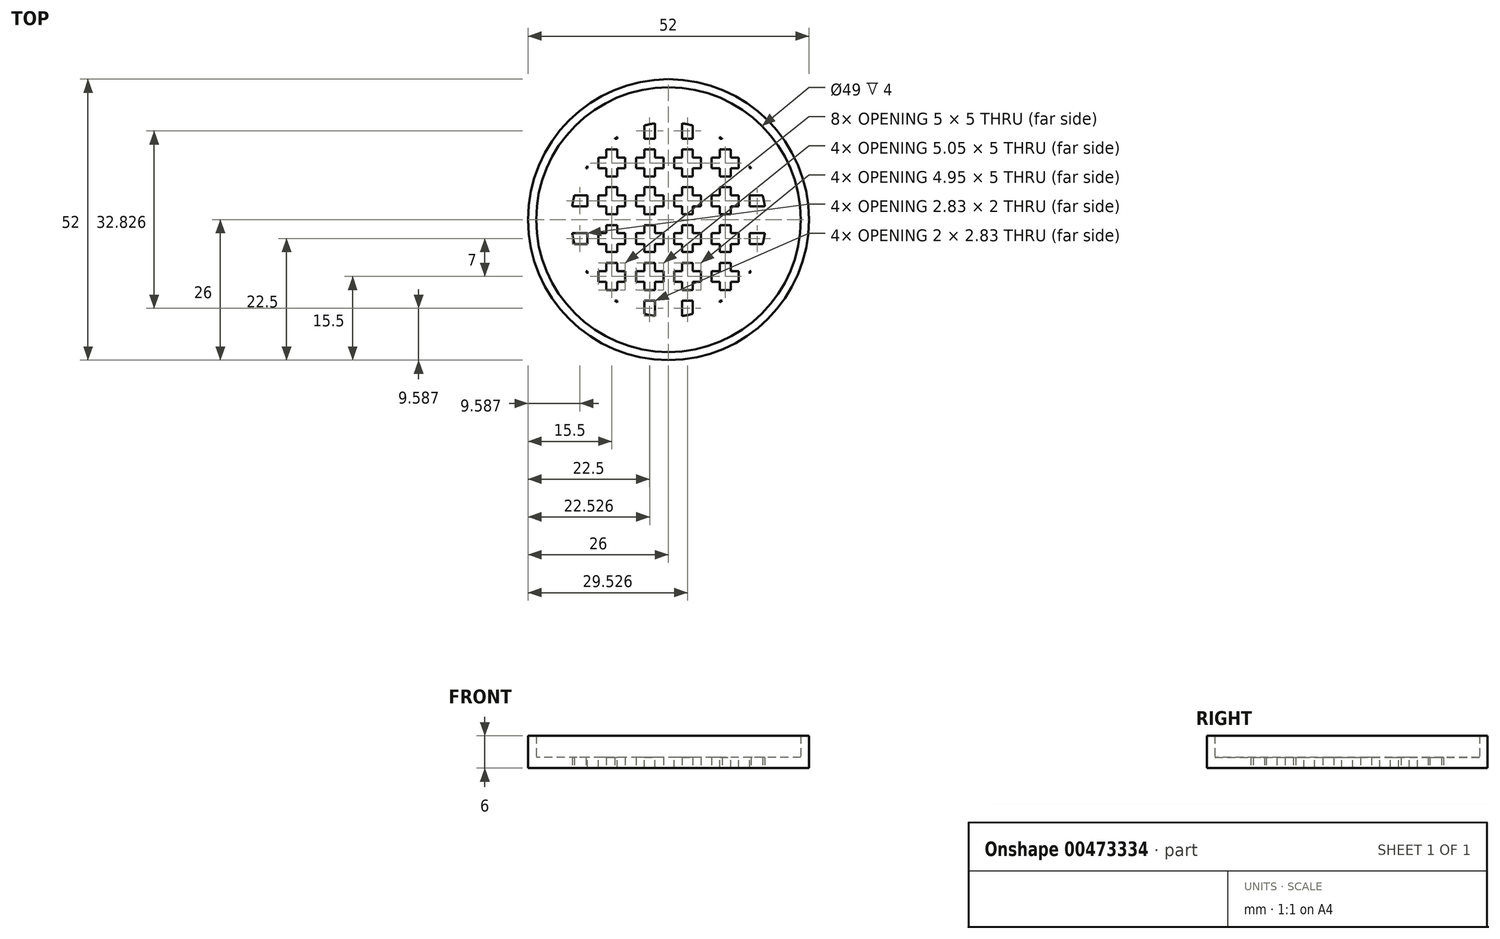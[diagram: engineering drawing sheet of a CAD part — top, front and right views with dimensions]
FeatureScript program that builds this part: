
annotation { "Feature Type Name" : "Feature", "Feature Type Description" : "" }
export const myFeature = defineFeature(function(context is Context, id is Id, definition is map)
    precondition{}
    {
        {
            var Q0;
            Q0=qCreatedBy(makeId("Top.planeOp"),FACE);
            var sketch = newSketch(context, id + "F0", { "sketchPlane" : qUnion([Q0])});
            skCircle(sketch, "E0", {"center": v(0, 0) * mm, "radius": 18 * mm});
            skSolve(sketch);
        }
        {
            var Q0;
            Q0 = qSketchRegion(id + "F0", true);
            extrude(context, id + "F1", {"entities" : qUnion([Q0]), "depth" : 2 * mm});
        }
        {
            var Q0;
            Q0=qCreatedBy(makeId("Top.planeOp"),FACE);
            var sketch = newSketch(context, id + "F2", { "sketchPlane" : qUnion([Q0])});
            skLineSegment(sketch, "E1.bottom", {"start": v(-11.5, 15.29) * mm, "end": v(-9.5, 15.29) * mm});
            skLineSegment(sketch, "E1.top", {"start": v(-11.5, -15.29) * mm, "end": v(-9.5, -15.29) * mm});
            skLineSegment(sketch, "E1.left", {"start": v(-11.5, 15.29) * mm, "end": v(-11.5, -15.29) * mm});
            skLineSegment(sketch, "E1.right", {"start": v(-9.5, 15.29) * mm, "end": v(-9.5, -15.29) * mm});
            skLineSegment(sketch, "E2.bottom", {"start": v(-4.5, 18) * mm, "end": v(-2.5, 18) * mm});
            skLineSegment(sketch, "E2.top", {"start": v(-4.5, -18) * mm, "end": v(-2.5, -18) * mm});
            skLineSegment(sketch, "E2.left", {"start": v(-4.5, 18) * mm, "end": v(-4.5, -18) * mm});
            skLineSegment(sketch, "E2.right", {"start": v(-2.5, 18) * mm, "end": v(-2.5, -18) * mm});
            skLineSegment(sketch, "E3.bottom", {"start": v(2.5, 18) * mm, "end": v(4.5, 18) * mm});
            skLineSegment(sketch, "E3.top", {"start": v(2.5, -18) * mm, "end": v(4.5, -18) * mm});
            skLineSegment(sketch, "E3.left", {"start": v(2.5, 18) * mm, "end": v(2.5, -18) * mm});
            skLineSegment(sketch, "E3.right", {"start": v(4.5, 18) * mm, "end": v(4.5, -18) * mm});
            skLineSegment(sketch, "E4.bottom", {"start": v(9.5, 15.29) * mm, "end": v(11.5, 15.29) * mm});
            skLineSegment(sketch, "E4.top", {"start": v(9.5, -15.29) * mm, "end": v(11.5, -15.29) * mm});
            skLineSegment(sketch, "E4.left", {"start": v(9.5, 15.29) * mm, "end": v(9.5, -15.29) * mm});
            skLineSegment(sketch, "E4.right", {"start": v(11.5, 15.29) * mm, "end": v(11.5, -15.29) * mm});
            skLineSegment(sketch, "E5.bottom", {"start": v(-15.29, -9.5) * mm, "end": v(15.29, -9.5) * mm});
            skLineSegment(sketch, "E5.top", {"start": v(-15.29, -11.5) * mm, "end": v(15.29, -11.5) * mm});
            skLineSegment(sketch, "E5.left", {"start": v(-15.29, -9.5) * mm, "end": v(-15.29, -11.5) * mm});
            skLineSegment(sketch, "E5.right", {"start": v(15.29, -9.5) * mm, "end": v(15.29, -11.5) * mm});
            skLineSegment(sketch, "E6.bottom", {"start": v(-17.83, -2.5) * mm, "end": v(17.83, -2.5) * mm});
            skLineSegment(sketch, "E6.top", {"start": v(-17.83, -4.5) * mm, "end": v(17.83, -4.5) * mm});
            skLineSegment(sketch, "E6.left", {"start": v(-17.83, -2.5) * mm, "end": v(-17.83, -4.5) * mm});
            skLineSegment(sketch, "E6.right", {"start": v(17.83, -2.5) * mm, "end": v(17.83, -4.5) * mm});
            skLineSegment(sketch, "E7.bottom", {"start": v(-21.9, 4.5) * mm, "end": v(17.83, 4.5) * mm});
            skLineSegment(sketch, "E7.top", {"start": v(-21.9, 2.5) * mm, "end": v(17.83, 2.5) * mm});
            skLineSegment(sketch, "E7.left", {"start": v(-21.9, 4.5) * mm, "end": v(-21.9, 2.5) * mm});
            skLineSegment(sketch, "E7.right", {"start": v(17.83, 4.5) * mm, "end": v(17.83, 2.5) * mm});
            skLineSegment(sketch, "E8.bottom", {"start": v(-15.29, 11.5) * mm, "end": v(15.29, 11.5) * mm});
            skLineSegment(sketch, "E8.top", {"start": v(-15.29, 9.5) * mm, "end": v(15.29, 9.5) * mm});
            skLineSegment(sketch, "E8.left", {"start": v(-15.29, 11.5) * mm, "end": v(-15.29, 9.5) * mm});
            skLineSegment(sketch, "E8.right", {"start": v(15.29, 11.5) * mm, "end": v(15.29, 9.5) * mm});
            skSolve(sketch);
        }
        {
            var Q0;
            Q0 = qSketchRegion(id + "F2", true);
            extrude(context, id + "F3", {"entities" : qUnion([Q0]), "operationType" : NewBodyOperationType.REMOVE, "depth" : 25 * mm});
        }
        {
            var Q0;
            Q0=qCreatedBy(makeId("Top.planeOp"),FACE);
            var sketch = newSketch(context, id + "F4", { "sketchPlane" : qUnion([Q0])});
            skCircle(sketch, "E9", {"center": v(0, 0) * mm, "radius": 26 * mm});
            skCircle(sketch, "E10", {"center": v(0, 0) * mm, "radius": 18 * mm});
            skSolve(sketch);
        }
        {
            var Q0;
            Q0 = qSketchRegion(id + "F4", true);
            extrude(context, id + "F5", {"entities" : qUnion([Q0]), "operationType" : NewBodyOperationType.ADD, "depth" : 2 * mm});
        }
        {
            var Q0;
            Q0=qCreatedBy(makeId("Top.planeOp"),FACE);
            var sketch = newSketch(context, id + "F6", { "sketchPlane" : qUnion([Q0])});
            skLineSegment(sketch, "E11.bottom", {"start": v(-4.29, 9.5) * mm, "end": v(-2.29, 9.5) * mm});
            skLineSegment(sketch, "E11.top", {"start": v(-4.29, -5.46) * mm, "end": v(-2.29, -5.46) * mm});
            skLineSegment(sketch, "E11.left", {"start": v(-4.29, 9.5) * mm, "end": v(-4.29, -5.46) * mm});
            skLineSegment(sketch, "E11.right", {"start": v(-2.29, 9.5) * mm, "end": v(-2.29, -5.46) * mm});
            skSolve(sketch);
        }
        {
            var Q0;
            Q0 = qSketchRegion(id + "F6", true);
            extrude(context, id + "F7", {"entities" : qUnion([Q0]), "operationType" : NewBodyOperationType.REMOVE, "oppositeDirection" : true, "depth" : 25 * mm});
        }
        {
            var Q0;
            Q0=qCreatedBy(makeId("Top.planeOp"),FACE);
            var sketch = newSketch(context, id + "F8", { "sketchPlane" : qUnion([Q0])});
            skLineSegment(sketch, "E12.bottom", {"start": v(-4.5, 11.5) * mm, "end": v(-2.5, 11.5) * mm});
            skLineSegment(sketch, "E12.top", {"start": v(-4.5, -11.5) * mm, "end": v(-2.5, -11.5) * mm});
            skLineSegment(sketch, "E12.left", {"start": v(-4.5, 11.5) * mm, "end": v(-4.5, -11.5) * mm});
            skLineSegment(sketch, "E12.right", {"start": v(-2.5, 11.5) * mm, "end": v(-2.5, -11.5) * mm});
            skLineSegment(sketch, "E13.bottom", {"start": v(2.5, 11.5) * mm, "end": v(4.5, 11.5) * mm});
            skLineSegment(sketch, "E13.top", {"start": v(2.5, -11.5) * mm, "end": v(4.5, -11.5) * mm});
            skLineSegment(sketch, "E13.left", {"start": v(2.5, 11.5) * mm, "end": v(2.5, -11.5) * mm});
            skLineSegment(sketch, "E13.right", {"start": v(4.5, 11.5) * mm, "end": v(4.5, -11.5) * mm});
            skLineSegment(sketch, "E14.bottom", {"start": v(-11.5, 4.5) * mm, "end": v(11.5, 4.5) * mm});
            skLineSegment(sketch, "E14.top", {"start": v(-11.5, 2.5) * mm, "end": v(11.5, 2.5) * mm});
            skLineSegment(sketch, "E14.left", {"start": v(-11.5, 4.5) * mm, "end": v(-11.5, 2.5) * mm});
            skLineSegment(sketch, "E14.right", {"start": v(11.5, 4.5) * mm, "end": v(11.5, 2.5) * mm});
            skLineSegment(sketch, "E15.bottom", {"start": v(-11.5, -2.5) * mm, "end": v(11.5, -2.5) * mm});
            skLineSegment(sketch, "E15.top", {"start": v(-11.5, -4.5) * mm, "end": v(11.5, -4.5) * mm});
            skLineSegment(sketch, "E15.left", {"start": v(-11.5, -2.5) * mm, "end": v(-11.5, -4.5) * mm});
            skLineSegment(sketch, "E15.right", {"start": v(11.5, -2.5) * mm, "end": v(11.5, -4.5) * mm});
            skSolve(sketch);
        }
        {
            var Q0;
            Q0 = qSketchRegion(id + "F8", true);
            extrude(context, id + "F9", {"entities" : qUnion([Q0]), "operationType" : NewBodyOperationType.REMOVE, "depth" : 25 * mm});
        }
        {
            var Q0;
            Q0=qCreatedBy(makeId("Top.planeOp"),FACE);
            var sketch = newSketch(context, id + "F10", { "sketchPlane" : qUnion([Q0])});
            skLineSegment(sketch, "E16.bottom", {"start": v(-15, 8) * mm, "end": v(15.3, 8) * mm});
            skLineSegment(sketch, "E16.top", {"start": v(-15, 6) * mm, "end": v(15.3, 6) * mm});
            skLineSegment(sketch, "E16.left", {"start": v(-15, 8) * mm, "end": v(-15, 6) * mm});
            skLineSegment(sketch, "E16.right", {"start": v(15.3, 8) * mm, "end": v(15.3, 6) * mm});
            skLineSegment(sketch, "E17.bottom", {"start": v(-13.95, 1) * mm, "end": v(13.98, 1) * mm});
            skLineSegment(sketch, "E17.top", {"start": v(-13.95, -1) * mm, "end": v(13.98, -1) * mm});
            skLineSegment(sketch, "E17.left", {"start": v(-13.95, 1) * mm, "end": v(-13.95, -1) * mm});
            skLineSegment(sketch, "E17.right", {"start": v(13.98, 1) * mm, "end": v(13.98, -1) * mm});
            skLineSegment(sketch, "E18.bottom", {"start": v(-13.75, -6) * mm, "end": v(12.64, -6) * mm});
            skLineSegment(sketch, "E18.top", {"start": v(-13.75, -8) * mm, "end": v(12.64, -8) * mm});
            skLineSegment(sketch, "E18.left", {"start": v(-13.75, -6) * mm, "end": v(-13.75, -8) * mm});
            skLineSegment(sketch, "E18.right", {"start": v(12.64, -6) * mm, "end": v(12.64, -8) * mm});
            skLineSegment(sketch, "E19.bottom", {"start": v(-10.45, -13) * mm, "end": v(12.45, -13) * mm});
            skLineSegment(sketch, "E19.top", {"start": v(-10.45, -15) * mm, "end": v(12.45, -15) * mm});
            skLineSegment(sketch, "E19.left", {"start": v(-10.45, -13) * mm, "end": v(-10.45, -15) * mm});
            skLineSegment(sketch, "E19.right", {"start": v(12.45, -13) * mm, "end": v(12.45, -15) * mm});
            skLineSegment(sketch, "E20.bottom", {"start": v(-12.51, 13) * mm, "end": v(12.95, 13) * mm});
            skLineSegment(sketch, "E20.top", {"start": v(-12.51, 15) * mm, "end": v(12.95, 15) * mm});
            skLineSegment(sketch, "E20.left", {"start": v(-12.51, 13) * mm, "end": v(-12.51, 15) * mm});
            skLineSegment(sketch, "E20.right", {"start": v(12.95, 13) * mm, "end": v(12.95, 15) * mm});
            skLineSegment(sketch, "E21.bottom", {"start": v(-6, 16.97) * mm, "end": v(-8, 16.97) * mm});
            skLineSegment(sketch, "E21.top", {"start": v(-6, -16.97) * mm, "end": v(-8, -16.97) * mm});
            skLineSegment(sketch, "E21.left", {"start": v(-6, 16.97) * mm, "end": v(-6, -16.97) * mm});
            skLineSegment(sketch, "E21.right", {"start": v(-8, 16.97) * mm, "end": v(-8, -16.97) * mm});
            skPoint(sketch, "E22.oppositeSnap0", {"position": v(1, -15) * mm});
            skLineSegment(sketch, "E22.bottom", {"start": v(-1, 17.97) * mm, "end": v(1, 17.97) * mm});
            skLineSegment(sketch, "E22.top", {"start": v(-1, -17.97) * mm, "end": v(1, -17.97) * mm});
            skLineSegment(sketch, "E22.left", {"start": v(-1, 17.97) * mm, "end": v(-1, -17.97) * mm});
            skLineSegment(sketch, "E22.right", {"start": v(1, 17.97) * mm, "end": v(1, -17.97) * mm});
            skLineSegment(sketch, "E23.bottom", {"start": v(6, 16.97) * mm, "end": v(8, 16.97) * mm});
            skLineSegment(sketch, "E23.top", {"start": v(6, -16.97) * mm, "end": v(8, -16.97) * mm});
            skLineSegment(sketch, "E23.left", {"start": v(6, 16.97) * mm, "end": v(6, -16.97) * mm});
            skLineSegment(sketch, "E23.right", {"start": v(8, 16.97) * mm, "end": v(8, -16.97) * mm});
            skLineSegment(sketch, "E24.bottom", {"start": v(13, -12.45) * mm, "end": v(15, -12.45) * mm});
            skLineSegment(sketch, "E24.top", {"start": v(13, 12.45) * mm, "end": v(15, 12.45) * mm});
            skLineSegment(sketch, "E24.left", {"start": v(13, -12.45) * mm, "end": v(13, 12.45) * mm});
            skLineSegment(sketch, "E24.right", {"start": v(15, -12.45) * mm, "end": v(15, 12.45) * mm});
            skLineSegment(sketch, "E25.bottom", {"start": v(-13, -12.45) * mm, "end": v(-15, -12.45) * mm});
            skLineSegment(sketch, "E25.top", {"start": v(-13, 12.45) * mm, "end": v(-15, 12.45) * mm});
            skLineSegment(sketch, "E25.left", {"start": v(-13, -12.45) * mm, "end": v(-13, 12.45) * mm});
            skLineSegment(sketch, "E25.right", {"start": v(-15, -12.45) * mm, "end": v(-15, 12.45) * mm});
            skSolve(sketch);
        }
        {
            var Q0;
            Q0 = qSketchRegion(id + "F10", true);
            extrude(context, id + "F11", {"entities" : qUnion([Q0]), "operationType" : NewBodyOperationType.ADD, "depth" : 2 * mm});
        }
        {
            var Q0;
            Q0=qCreatedBy(makeId("Top.planeOp"),FACE);
            var sketch = newSketch(context, id + "F12", { "sketchPlane" : qUnion([Q0])});
            skLineSegment(sketch, "E26.bottom", {"start": v(-8, 9.5) * mm, "end": v(-6, 9.5) * mm});
            skLineSegment(sketch, "E26.top", {"start": v(-8, -7.23) * mm, "end": v(-6, -7.23) * mm});
            skLineSegment(sketch, "E26.left", {"start": v(-8, 9.5) * mm, "end": v(-8, -7.23) * mm});
            skLineSegment(sketch, "E26.right", {"start": v(-6, 9.5) * mm, "end": v(-6, -7.23) * mm});
            skLineSegment(sketch, "E27.bottom", {"start": v(-0.95, -11.5) * mm, "end": v(1.05, -11.5) * mm});
            skLineSegment(sketch, "E27.top", {"start": v(-0.95, 12.4) * mm, "end": v(1.05, 12.4) * mm});
            skLineSegment(sketch, "E27.left", {"start": v(-0.95, -11.5) * mm, "end": v(-0.95, 12.4) * mm});
            skLineSegment(sketch, "E27.right", {"start": v(1.05, -11.5) * mm, "end": v(1.05, 12.4) * mm});
            skLineSegment(sketch, "E28.bottom", {"start": v(6, 6) * mm, "end": v(8, 6) * mm});
            skLineSegment(sketch, "E28.top", {"start": v(6, -1.53) * mm, "end": v(8, -1.53) * mm});
            skLineSegment(sketch, "E28.left", {"start": v(6, 6) * mm, "end": v(6, -1.53) * mm});
            skLineSegment(sketch, "E28.right", {"start": v(8, 6) * mm, "end": v(8, -1.53) * mm});
            skPoint(sketch, "E29.oppositeSnap0", {"position": v(7, 6) * mm});
            skLineSegment(sketch, "E29.bottom", {"start": v(-9.5, 8) * mm, "end": v(10.5, 8) * mm});
            skLineSegment(sketch, "E29.top", {"start": v(-9.5, 6) * mm, "end": v(10.5, 6) * mm});
            skLineSegment(sketch, "E29.left", {"start": v(-9.5, 8) * mm, "end": v(-9.5, 6) * mm});
            skLineSegment(sketch, "E29.right", {"start": v(10.5, 8) * mm, "end": v(10.5, 6) * mm});
            skLineSegment(sketch, "E30.bottom", {"start": v(-12.5, 1) * mm, "end": v(11.5, 1) * mm});
            skLineSegment(sketch, "E30.top", {"start": v(-12.5, -1) * mm, "end": v(11.5, -1) * mm});
            skLineSegment(sketch, "E30.left", {"start": v(-12.5, 1) * mm, "end": v(-12.5, -1) * mm});
            skLineSegment(sketch, "E30.right", {"start": v(11.5, 1) * mm, "end": v(11.5, -1) * mm});
            skLineSegment(sketch, "E31.bottom", {"start": v(-9.5, -6) * mm, "end": v(10.5, -6) * mm});
            skLineSegment(sketch, "E31.top", {"start": v(-9.5, -8) * mm, "end": v(10.5, -8) * mm});
            skLineSegment(sketch, "E31.left", {"start": v(-9.5, -6) * mm, "end": v(-9.5, -8) * mm});
            skLineSegment(sketch, "E31.right", {"start": v(10.5, -6) * mm, "end": v(10.5, -8) * mm});
            skSolve(sketch);
        }
        {
            var Q0;
            Q0 = qSketchRegion(id + "F12", true);
            extrude(context, id + "F13", {"entities" : qUnion([Q0]), "operationType" : NewBodyOperationType.ADD, "depth" : 2 * mm});
        }
        {
            var Q0;
            Q0=qCreatedBy(makeId("Top.planeOp"),FACE);
            var sketch = newSketch(context, id + "F14", { "sketchPlane" : qUnion([Q0])});
            skLineSegment(sketch, "E32.bottom", {"start": v(-0.95, 5.83) * mm, "end": v(1.05, 5.83) * mm});
            skLineSegment(sketch, "E32.top", {"start": v(-0.95, 0) * mm, "end": v(1.05, 0) * mm});
            skLineSegment(sketch, "E32.left", {"start": v(-0.95, 5.83) * mm, "end": v(-0.95, 0) * mm});
            skLineSegment(sketch, "E32.right", {"start": v(1.05, 5.83) * mm, "end": v(1.05, 0) * mm});
            skLineSegment(sketch, "E33.bottom", {"start": v(-6.66, 1) * mm, "end": v(-1.89, 1) * mm});
            skLineSegment(sketch, "E33.top", {"start": v(-6.66, -1) * mm, "end": v(-1.89, -1) * mm});
            skLineSegment(sketch, "E33.left", {"start": v(-6.66, 1) * mm, "end": v(-6.66, -1) * mm});
            skLineSegment(sketch, "E33.right", {"start": v(-1.89, 1) * mm, "end": v(-1.89, -1) * mm});
            skLineSegment(sketch, "E34.bottom", {"start": v(-7.18, -13) * mm, "end": v(-12.23, -13) * mm});
            skLineSegment(sketch, "E34.top", {"start": v(-7.18, -15) * mm, "end": v(-12.23, -15) * mm});
            skLineSegment(sketch, "E34.left", {"start": v(-7.18, -13) * mm, "end": v(-7.18, -15) * mm});
            skLineSegment(sketch, "E34.right", {"start": v(-12.23, -13) * mm, "end": v(-12.23, -15) * mm});
            skSolve(sketch);
        }
        {
            var Q0;
            Q0 = qSketchRegion(id + "F14", true);
            extrude(context, id + "F15", {"entities" : qUnion([Q0]), "operationType" : NewBodyOperationType.ADD, "depth" : 2 * mm});
        }
        {
            var Q0;
            {var subQ0=sQuery(id+"F2.wireOp",EDGE,"E6.top");var subQ5=sQuery(id+"F2.wireOp",EDGE,"E6.bottom");var subQ7=sQuery(id+"F2.wireOp",EDGE,"E7.top");var subQ9=sQuery(id+"F2.wireOp",EDGE,"E7.bottom");var subQ11=sQuery(id+"F2.wireOp",EDGE,"E8.top");var subQ15=sQuery(id+"F2.wireOp",EDGE,"E3.right");var subQ19=sQuery(id+"F2.wireOp",EDGE,"E2.right");var subQ23=sQuery(id+"F2.wireOp",EDGE,"E1.right");var subQ27=sQuery(id+"F8.wireOp",EDGE,"E13.right");var subQ28=sQuery(id+"F8.wireOp",EDGE,"E13.top");var subQ32=makeQuery(id+"F2.imprint","INTERSECT",VERTEX,{"derivedFrom":[subQ23,subQ0]});var subQ33=makeQuery(id+"F2.imprint","INTERSECT",VERTEX,{"derivedFrom":[subQ23,subQ5]});var subQ34=makeQuery(id+"F2.imprint","INTERSECT",VERTEX,{"derivedFrom":[subQ23,subQ7]});var subQ35=makeQuery(id+"F2.imprint","INTERSECT",VERTEX,{"derivedFrom":[subQ23,subQ9]});var subQ36=makeQuery(id+"F2.imprint","INTERSECT",VERTEX,{"derivedFrom":[subQ23,subQ11]});var subQ37=makeQuery(id+"F3.opExtrude","SWEPT_FACE",FACE,{"disambiguationData":[OSD([subQ23]),TDD([makeQuery(id+"F2.imprint","IMPRINT",EDGE,{"disambiguationData":[TD([[subQ36,-1.0]])],"derivedFrom":subQ23}),makeQuery(id+"F2.imprint","IMPRINT",EDGE,{"disambiguationData":[TD([[subQ35,-1.0]])],"derivedFrom":subQ23}),makeQuery(id+"F2.imprint","IMPRINT",EDGE,{"disambiguationData":[TD([[subQ34,-1.0]])],"derivedFrom":subQ23}),makeQuery(id+"F2.imprint","IMPRINT",EDGE,{"disambiguationData":[TD([[subQ33,-1.0]])],"derivedFrom":subQ23}),makeQuery(id+"F2.imprint","IMPRINT",EDGE,{"disambiguationData":[TD([[subQ32,-1.0]])],"derivedFrom":subQ23})])]});var subQ43=sQuery(id+"F0.wireOp",EDGE,"E0");var subQ44=makeQuery(id+"F1.opExtrude","CAP_FACE",FACE,{"disambiguationData":[OSD([subQ43])],"isStart":false});var subQ45=makeQuery(id+"F3.boolean.opBoolean","SPLIT",FACE,{"disambiguationData":[TD([subQ37])],"derivedFrom":subQ44});var subQ47=sQuery(id+"F8.wireOp",EDGE,"E13.bottom");var subQ52=sQuery(id+"F8.wireOp",EDGE,"E12.left");var subQ53=sQuery(id+"F8.wireOp",EDGE,"E12.top");var subQ58=sQuery(id+"F8.wireOp",EDGE,"E12.bottom");var subQ59=sQuery(id+"F8.wireOp",EDGE,"E14.top");var subQ60=makeQuery(id+"F8.imprint","INTERSECT",VERTEX,{"derivedFrom":[subQ27,subQ59]});var subQ64=sQuery(id+"F2.wireOp",EDGE,"E4.right");var subQ65=makeQuery(id+"F2.imprint","INTERSECT",VERTEX,{"derivedFrom":[subQ64,subQ0]});var subQ69=makeQuery(id+"F2.imprint","INTERSECT",VERTEX,{"derivedFrom":[subQ64,subQ7]});var subQ72=makeQuery(id+"F2.imprint","INTERSECT",VERTEX,{"derivedFrom":[subQ64,subQ11]});var subQ75=sQuery(id+"F2.wireOp",EDGE,"E3.top");var subQ78=sQuery(id+"F2.wireOp",EDGE,"E4.top");var subQ80=sQuery(id+"F2.wireOp",EDGE,"E3.bottom");var subQ83=sQuery(id+"F2.wireOp",EDGE,"E4.bottom");var subQ85=sQuery(id+"F2.wireOp",EDGE,"E2.top");var subQ88=sQuery(id+"F2.wireOp",EDGE,"E2.bottom");var subQ91=sQuery(id+"F2.wireOp",EDGE,"E1.top");var subQ96=sQuery(id+"F2.wireOp",EDGE,"E1.bottom");var subQ97=sQuery(id+"F2.wireOp",EDGE,"E1.left");var subQ98=makeQuery(id+"F2.imprint","INTERSECT",VERTEX,{"derivedFrom":[subQ97,subQ0]});var subQ103=makeQuery(id+"F2.imprint","INTERSECT",VERTEX,{"derivedFrom":[subQ97,subQ7]});var subQ105=makeQuery(id+"F2.imprint","INTERSECT",VERTEX,{"derivedFrom":[subQ97,subQ11]});var subQ112=sQuery(id+"F8.wireOp",EDGE,"E12.right");var subQ118=makeQuery(id+"F8.imprint","INTERSECT",VERTEX,{"derivedFrom":[subQ52,subQ59]});var subQ120=makeQuery(id+"F8.imprint","INTERSECT",VERTEX,{"derivedFrom":[subQ112,subQ59]});Q0=makeQuery(id+"F15.boolean.opBoolean","MERGE",FACE,{"derivedFrom":[makeQuery(id+"F13.boolean.opBoolean","MERGE",FACE,{"derivedFrom":[makeQuery(id+"F9.boolean.opBoolean","SPLIT",FACE,{"disambiguationData":[TD([makeQuery(id+"F9.opExtrude","SWEPT_FACE",FACE,{"disambiguationData":[OSD([subQ112]),TDD([makeQuery(id+"F8.imprint","IMPRINT",EDGE,{"disambiguationData":[TD([[subQ120,-1.0]])],"derivedFrom":subQ112})])]})])],"derivedFrom":subQ45}),makeQuery(id+"F9.boolean.opBoolean","SPLIT",FACE,{"disambiguationData":[TD([makeQuery(id+"F9.opExtrude","SWEPT_FACE",FACE,{"disambiguationData":[OSD([subQ52]),TDD([makeQuery(id+"F8.imprint","IMPRINT",EDGE,{"disambiguationData":[TD([[subQ118,-1.0]])],"derivedFrom":subQ52})])]})])],"derivedFrom":subQ45}),makeQuery(id+"F9.boolean.opBoolean","SPLIT",FACE,{"disambiguationData":[TD([makeQuery(id+"F9.opExtrude","SWEPT_FACE",FACE,{"disambiguationData":[OSD([subQ112]),TDD([makeQuery(id+"F8.imprint","IMPRINT",EDGE,{"disambiguationData":[TD([[makeQuery(id+"F8.imprint","INTERSECT",VERTEX,{"derivedFrom":[subQ58,subQ112]}),-1.0]])],"derivedFrom":subQ112})])]})])],"derivedFrom":subQ45}),makeQuery(id+"F9.boolean.opBoolean","SPLIT",FACE,{"disambiguationData":[TD([makeQuery(id+"F9.opExtrude","SWEPT_FACE",FACE,{"disambiguationData":[OSD([subQ112]),TDD([makeQuery(id+"F8.imprint","IMPRINT",EDGE,{"disambiguationData":[TD([[makeQuery(id+"F8.imprint","INTERSECT",VERTEX,{"derivedFrom":[subQ53,subQ112]}),1.0]])],"derivedFrom":subQ112})])]})])],"derivedFrom":subQ45}),makeQuery(id+"F11.boolean.opBoolean","MERGE",FACE,{"derivedFrom":[makeQuery(id+"F5.boolean.opBoolean","MERGE",FACE,{"derivedFrom":[makeQuery(id+"F3.boolean.opBoolean","SPLIT",FACE,{"disambiguationData":[TD([makeQuery(id+"F3.opExtrude","SWEPT_FACE",FACE,{"disambiguationData":[OSD([subQ97]),TDD([makeQuery(id+"F2.imprint","IMPRINT",EDGE,{"disambiguationData":[TD([[makeQuery(id+"F2.imprint","INTERSECT",VERTEX,{"derivedFrom":[subQ96,subQ97]}),-1.0]])],"derivedFrom":subQ97})])]})])],"derivedFrom":subQ44}),makeQuery(id+"F3.boolean.opBoolean","SPLIT",FACE,{"disambiguationData":[TD([makeQuery(id+"F3.opExtrude","SWEPT_FACE",FACE,{"disambiguationData":[OSD([subQ97]),TDD([makeQuery(id+"F2.imprint","IMPRINT",EDGE,{"disambiguationData":[TD([[makeQuery(id+"F2.imprint","INTERSECT",VERTEX,{"derivedFrom":[subQ91,subQ97]}),1.0]])],"derivedFrom":subQ97})])]})])],"derivedFrom":subQ44}),makeQuery(id+"F3.boolean.opBoolean","SPLIT",FACE,{"disambiguationData":[TD([makeQuery(id+"F3.opExtrude","SWEPT_FACE",FACE,{"disambiguationData":[OSD([subQ64]),TDD([makeQuery(id+"F2.imprint","IMPRINT",EDGE,{"disambiguationData":[TD([[makeQuery(id+"F2.imprint","INTERSECT",VERTEX,{"derivedFrom":[subQ83,subQ64]}),-1.0]])],"derivedFrom":subQ64})])]})])],"derivedFrom":subQ44}),makeQuery(id+"F3.boolean.opBoolean","SPLIT",FACE,{"disambiguationData":[TD([makeQuery(id+"F3.opExtrude","SWEPT_FACE",FACE,{"disambiguationData":[OSD([subQ64]),TDD([makeQuery(id+"F2.imprint","IMPRINT",EDGE,{"disambiguationData":[TD([[makeQuery(id+"F2.imprint","INTERSECT",VERTEX,{"derivedFrom":[subQ78,subQ64]}),1.0]])],"derivedFrom":subQ64})])]})])],"derivedFrom":subQ44}),makeQuery(id+"F3.boolean.opBoolean","SPLIT",FACE,{"disambiguationData":[TD([makeQuery(id+"F3.opExtrude","SWEPT_FACE",FACE,{"disambiguationData":[OSD([subQ97]),TDD([makeQuery(id+"F2.imprint","IMPRINT",EDGE,{"disambiguationData":[TD([[subQ105,-1.0]])],"derivedFrom":subQ97})])]})])],"derivedFrom":subQ44}),makeQuery(id+"F3.boolean.opBoolean","SPLIT",FACE,{"disambiguationData":[TD([makeQuery(id+"F3.opExtrude","SWEPT_FACE",FACE,{"disambiguationData":[OSD([subQ97]),TDD([makeQuery(id+"F2.imprint","IMPRINT",EDGE,{"disambiguationData":[TD([[subQ103,-1.0]])],"derivedFrom":subQ97})])]})])],"derivedFrom":subQ44}),makeQuery(id+"F3.boolean.opBoolean","SPLIT",FACE,{"disambiguationData":[TD([makeQuery(id+"F3.opExtrude","SWEPT_FACE",FACE,{"disambiguationData":[OSD([subQ97]),TDD([makeQuery(id+"F2.imprint","IMPRINT",EDGE,{"disambiguationData":[TD([[subQ98,-1.0]])],"derivedFrom":subQ97})])]})])],"derivedFrom":subQ44}),makeQuery(id+"F3.boolean.opBoolean","SPLIT",FACE,{"disambiguationData":[TD([makeQuery(id+"F3.opExtrude","SWEPT_FACE",FACE,{"disambiguationData":[OSD([subQ23]),TDD([makeQuery(id+"F2.imprint","IMPRINT",EDGE,{"disambiguationData":[TD([[makeQuery(id+"F2.imprint","INTERSECT",VERTEX,{"derivedFrom":[subQ96,subQ23]}),-1.0]])],"derivedFrom":subQ23})])]})])],"derivedFrom":subQ44}),makeQuery(id+"F3.boolean.opBoolean","SPLIT",FACE,{"disambiguationData":[TD([makeQuery(id+"F3.opExtrude","SWEPT_FACE",FACE,{"disambiguationData":[OSD([subQ23]),TDD([makeQuery(id+"F2.imprint","IMPRINT",EDGE,{"disambiguationData":[TD([[makeQuery(id+"F2.imprint","INTERSECT",VERTEX,{"derivedFrom":[subQ91,subQ23]}),1.0]])],"derivedFrom":subQ23})])]})])],"derivedFrom":subQ44}),makeQuery(id+"F3.boolean.opBoolean","SPLIT",FACE,{"disambiguationData":[TD([makeQuery(id+"F3.opExtrude","SWEPT_FACE",FACE,{"disambiguationData":[OSD([subQ19]),TDD([makeQuery(id+"F2.imprint","IMPRINT",EDGE,{"disambiguationData":[TD([[makeQuery(id+"F2.imprint","INTERSECT",VERTEX,{"derivedFrom":[subQ88,subQ19]}),-1.0]])],"derivedFrom":subQ19})])]})])],"derivedFrom":subQ44}),makeQuery(id+"F3.boolean.opBoolean","SPLIT",FACE,{"disambiguationData":[TD([makeQuery(id+"F3.opExtrude","SWEPT_FACE",FACE,{"disambiguationData":[OSD([subQ19]),TDD([makeQuery(id+"F2.imprint","IMPRINT",EDGE,{"disambiguationData":[TD([[makeQuery(id+"F2.imprint","INTERSECT",VERTEX,{"derivedFrom":[subQ85,subQ19]}),1.0]])],"derivedFrom":subQ19})])]})])],"derivedFrom":subQ44}),makeQuery(id+"F3.boolean.opBoolean","SPLIT",FACE,{"disambiguationData":[TD([makeQuery(id+"F3.opExtrude","SWEPT_FACE",FACE,{"disambiguationData":[OSD([subQ15]),TDD([makeQuery(id+"F2.imprint","IMPRINT",EDGE,{"disambiguationData":[TD([[makeQuery(id+"F2.imprint","INTERSECT",VERTEX,{"derivedFrom":[subQ80,subQ15]}),-1.0]])],"derivedFrom":subQ15})])]})])],"derivedFrom":subQ44}),makeQuery(id+"F3.boolean.opBoolean","SPLIT",FACE,{"disambiguationData":[TD([makeQuery(id+"F3.opExtrude","SWEPT_FACE",FACE,{"disambiguationData":[OSD([subQ15]),TDD([makeQuery(id+"F2.imprint","IMPRINT",EDGE,{"disambiguationData":[TD([[makeQuery(id+"F2.imprint","INTERSECT",VERTEX,{"derivedFrom":[subQ75,subQ15]}),1.0]])],"derivedFrom":subQ15})])]})])],"derivedFrom":subQ44}),makeQuery(id+"F3.boolean.opBoolean","SPLIT",FACE,{"disambiguationData":[TD([makeQuery(id+"F3.opExtrude","SWEPT_FACE",FACE,{"disambiguationData":[OSD([subQ64]),TDD([makeQuery(id+"F2.imprint","IMPRINT",EDGE,{"disambiguationData":[TD([[subQ72,-1.0]])],"derivedFrom":subQ64})])]})])],"derivedFrom":subQ44}),makeQuery(id+"F3.boolean.opBoolean","SPLIT",FACE,{"disambiguationData":[TD([makeQuery(id+"F3.opExtrude","SWEPT_FACE",FACE,{"disambiguationData":[OSD([subQ64]),TDD([makeQuery(id+"F2.imprint","IMPRINT",EDGE,{"disambiguationData":[TD([[subQ69,-1.0]])],"derivedFrom":subQ64})])]})])],"derivedFrom":subQ44}),makeQuery(id+"F3.boolean.opBoolean","SPLIT",FACE,{"disambiguationData":[TD([makeQuery(id+"F3.opExtrude","SWEPT_FACE",FACE,{"disambiguationData":[OSD([subQ64]),TDD([makeQuery(id+"F2.imprint","IMPRINT",EDGE,{"disambiguationData":[TD([[subQ65,-1.0]])],"derivedFrom":subQ64})])]})])],"derivedFrom":subQ44}),makeQuery(id+"F5.opExtrude","CAP_FACE",FACE,{"disambiguationData":[OSD([sQuery(id+"F4.wireOp",EDGE,"E9"),sQuery(id+"F4.wireOp",EDGE,"E10")])],"isStart":false})]}),makeQuery(id+"F9.boolean.opBoolean","SPLIT",FACE,{"disambiguationData":[TD([makeQuery(id+"F9.opExtrude","SWEPT_FACE",FACE,{"disambiguationData":[OSD([subQ27]),TDD([makeQuery(id+"F8.imprint","IMPRINT",EDGE,{"disambiguationData":[TD([[subQ60,-1.0]])],"derivedFrom":subQ27})])]})])],"derivedFrom":subQ45}),makeQuery(id+"F9.boolean.opBoolean","SPLIT",FACE,{"disambiguationData":[TD([makeQuery(id+"F9.opExtrude","SWEPT_FACE",FACE,{"disambiguationData":[OSD([subQ52]),TDD([makeQuery(id+"F8.imprint","IMPRINT",EDGE,{"disambiguationData":[TD([[makeQuery(id+"F8.imprint","INTERSECT",VERTEX,{"derivedFrom":[subQ58,subQ52]}),-1.0]])],"derivedFrom":subQ52})])]})])],"derivedFrom":subQ45}),makeQuery(id+"F9.boolean.opBoolean","SPLIT",FACE,{"disambiguationData":[TD([makeQuery(id+"F9.opExtrude","SWEPT_FACE",FACE,{"disambiguationData":[OSD([subQ52]),TDD([makeQuery(id+"F8.imprint","IMPRINT",EDGE,{"disambiguationData":[TD([[makeQuery(id+"F8.imprint","INTERSECT",VERTEX,{"derivedFrom":[subQ53,subQ52]}),1.0]])],"derivedFrom":subQ52})])]})])],"derivedFrom":subQ45}),makeQuery(id+"F9.boolean.opBoolean","SPLIT",FACE,{"disambiguationData":[TD([makeQuery(id+"F9.opExtrude","SWEPT_FACE",FACE,{"disambiguationData":[OSD([subQ27]),TDD([makeQuery(id+"F8.imprint","IMPRINT",EDGE,{"disambiguationData":[TD([[makeQuery(id+"F8.imprint","INTERSECT",VERTEX,{"derivedFrom":[subQ47,subQ27]}),-1.0]])],"derivedFrom":subQ27})])]})])],"derivedFrom":subQ45}),makeQuery(id+"F9.boolean.opBoolean","SPLIT",FACE,{"disambiguationData":[TD([makeQuery(id+"F9.opExtrude","SWEPT_FACE",FACE,{"disambiguationData":[OSD([subQ27]),TDD([makeQuery(id+"F8.imprint","IMPRINT",EDGE,{"disambiguationData":[TD([[makeQuery(id+"F8.imprint","INTERSECT",VERTEX,{"derivedFrom":[subQ28,subQ27]}),1.0]])],"derivedFrom":subQ27})])]})])],"derivedFrom":subQ45}),makeQuery(id+"F11.opExtrude","CAP_FACE",FACE,{"disambiguationData":[OSD([sQuery(id+"F10.wireOp",EDGE,"E16.bottom"),sQuery(id+"F10.wireOp",EDGE,"E16.top"),sQuery(id+"F10.wireOp",EDGE,"E16.right"),sQuery(id+"F10.wireOp",EDGE,"E17.bottom"),sQuery(id+"F10.wireOp",EDGE,"E17.top"),sQuery(id+"F10.wireOp",EDGE,"E17.left"),sQuery(id+"F10.wireOp",EDGE,"E18.bottom"),sQuery(id+"F10.wireOp",EDGE,"E18.top"),sQuery(id+"F10.wireOp",EDGE,"E18.right"),sQuery(id+"F10.wireOp",EDGE,"E19.bottom"),sQuery(id+"F10.wireOp",EDGE,"E19.top"),sQuery(id+"F10.wireOp",EDGE,"E19.left"),sQuery(id+"F10.wireOp",EDGE,"E19.right"),sQuery(id+"F10.wireOp",EDGE,"E20.bottom"),sQuery(id+"F10.wireOp",EDGE,"E20.top"),sQuery(id+"F10.wireOp",EDGE,"E20.left"),sQuery(id+"F10.wireOp",EDGE,"E20.right"),sQuery(id+"F10.wireOp",EDGE,"E21.bottom"),sQuery(id+"F10.wireOp",EDGE,"E21.top"),sQuery(id+"F10.wireOp",EDGE,"E21.left"),sQuery(id+"F10.wireOp",EDGE,"E21.right"),sQuery(id+"F10.wireOp",EDGE,"E22.bottom"),sQuery(id+"F10.wireOp",EDGE,"E22.top"),sQuery(id+"F10.wireOp",EDGE,"E22.left"),sQuery(id+"F10.wireOp",EDGE,"E22.right"),sQuery(id+"F10.wireOp",EDGE,"E23.bottom"),sQuery(id+"F10.wireOp",EDGE,"E23.top"),sQuery(id+"F10.wireOp",EDGE,"E23.left"),sQuery(id+"F10.wireOp",EDGE,"E23.right"),sQuery(id+"F10.wireOp",EDGE,"E24.bottom"),sQuery(id+"F10.wireOp",EDGE,"E24.top"),sQuery(id+"F10.wireOp",EDGE,"E24.left"),sQuery(id+"F10.wireOp",EDGE,"E24.right"),sQuery(id+"F10.wireOp",EDGE,"E25.bottom"),sQuery(id+"F10.wireOp",EDGE,"E25.top"),sQuery(id+"F10.wireOp",EDGE,"E25.left"),sQuery(id+"F10.wireOp",EDGE,"E25.right")])],"isStart":false})]}),makeQuery(id+"F13.opExtrude","CAP_FACE",FACE,{"disambiguationData":[OSD([sQuery(id+"F12.wireOp",EDGE,"E26.bottom"),sQuery(id+"F12.wireOp",EDGE,"E26.left"),sQuery(id+"F12.wireOp",EDGE,"E26.right"),sQuery(id+"F12.wireOp",EDGE,"E27.bottom"),sQuery(id+"F12.wireOp",EDGE,"E27.top"),sQuery(id+"F12.wireOp",EDGE,"E27.left"),sQuery(id+"F12.wireOp",EDGE,"E27.right"),sQuery(id+"F12.wireOp",EDGE,"E28.top"),sQuery(id+"F12.wireOp",EDGE,"E28.left"),sQuery(id+"F12.wireOp",EDGE,"E28.right"),sQuery(id+"F12.wireOp",EDGE,"E29.bottom"),sQuery(id+"F12.wireOp",EDGE,"E29.top"),sQuery(id+"F12.wireOp",EDGE,"E29.left"),sQuery(id+"F12.wireOp",EDGE,"E29.right"),sQuery(id+"F12.wireOp",EDGE,"E30.bottom"),sQuery(id+"F12.wireOp",EDGE,"E30.top"),sQuery(id+"F12.wireOp",EDGE,"E30.left"),sQuery(id+"F12.wireOp",EDGE,"E30.right"),sQuery(id+"F12.wireOp",EDGE,"E31.bottom"),sQuery(id+"F12.wireOp",EDGE,"E31.top"),sQuery(id+"F12.wireOp",EDGE,"E31.left"),sQuery(id+"F12.wireOp",EDGE,"E31.right")])],"isStart":false})]}),makeQuery(id+"F15.opExtrude","CAP_FACE",FACE,{"disambiguationData":[OSD([sQuery(id+"F14.wireOp",EDGE,"E32.bottom"),sQuery(id+"F14.wireOp",EDGE,"E32.top"),sQuery(id+"F14.wireOp",EDGE,"E32.left"),sQuery(id+"F14.wireOp",EDGE,"E32.right")])],"isStart":false}),makeQuery(id+"F15.opExtrude","CAP_FACE",FACE,{"disambiguationData":[OSD([sQuery(id+"F14.wireOp",EDGE,"E33.bottom"),sQuery(id+"F14.wireOp",EDGE,"E33.top"),sQuery(id+"F14.wireOp",EDGE,"E33.left"),sQuery(id+"F14.wireOp",EDGE,"E33.right")])],"isStart":false}),makeQuery(id+"F15.opExtrude","CAP_FACE",FACE,{"disambiguationData":[OSD([sQuery(id+"F14.wireOp",EDGE,"E34.bottom"),sQuery(id+"F14.wireOp",EDGE,"E34.top"),sQuery(id+"F14.wireOp",EDGE,"E34.left"),sQuery(id+"F14.wireOp",EDGE,"E34.right")])],"isStart":false})]});}
            var sketch = newSketch(context, id + "F16", { "sketchPlane" : qUnion([Q0])});
            skCircle(sketch, "E35", {"center": v(0, 0) * mm, "radius": 26 * mm});
            skCircle(sketch, "E36", {"center": v(0, 0) * mm, "radius": 24.5 * mm});
            skSolve(sketch);
        }
        {
            var Q0;
            Q0 = qSketchRegion(id + "F16", true);
            extrude(context, id + "F17", {"entities" : qUnion([Q0]), "operationType" : NewBodyOperationType.ADD, "depth" : 4 * mm});
        }
    });
